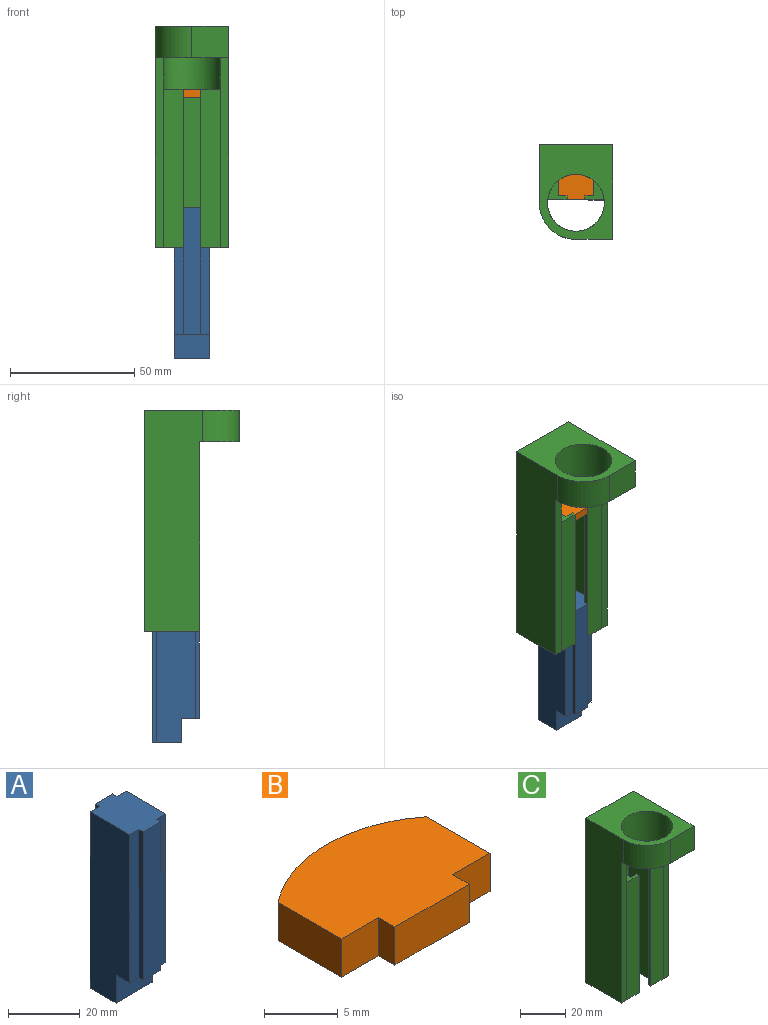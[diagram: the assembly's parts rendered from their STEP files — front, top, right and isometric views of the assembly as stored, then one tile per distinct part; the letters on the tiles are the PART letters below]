
ASSEMBLY  parts=3 mates=2
PART A: 18 faces, bbox 14.2x19x60.3 mm
  f0: plane 60.33x1.63mm, normal (-1,0,0), area 98.1mm2, adj f1,f11,f12,f15
  f1: plane 60.33x3.58mm, normal (0,1,0), area 216mm2, adj f0,f2,f12,f15
  f2: plane 60.33x15.75mm, normal (-1,0,0), area 897.7mm2, adj f1,f3,f12,f13,f14,f15
  f3: plane 50.8x3.58mm, normal (0,-1,0), area 181.9mm2, adj f2,f4,f12,f13
  f4: plane 50.8x1.63mm, normal (-1,0,0), area 82.6mm2, adj f3,f5,f12,f13
  f5: plane 50.8x7.06mm, normal (0,-1,0), area 358.7mm2, adj f4,f6,f12,f13
  f6: plane 50.8x1.63mm, normal (1,0,0), area 82.6mm2, adj f5,f7,f12,f13
  f7: plane 50.8x3.58mm, normal (0,-1,0), area 181.9mm2, adj f6,f8,f12,f13
  f8: plane 60.33x15.75mm, normal (1,0,0), area 897.7mm2, adj f7,f9,f12,f13,f14,f15
  f9: plane 60.33x3.58mm, normal (0,1,0), area 216mm2, adj f8,f10,f12,f15
  f10: plane 60.33x1.63mm, normal (1,0,0), area 98.1mm2, adj f9,f11,f12,f15
  f11: plane 60.33x7.06mm, normal (0,1,0), area 426mm2, adj f0,f10,f12,f15
  f12: plane 19x14.22mm, normal (0,0,1), area 247mm2, adj f0,f1,f2,f3,f4,f5,f6,f7
  f13: plane 14.22x7.11mm, normal (0,0,-1), area 81.6mm2, adj f2,f3,f4,f5,f6,f7,f8,f14
  f14: plane 14.22x9.53mm, normal (0,-1,0), area 135.5mm2, adj f2,f8,f13,f15
  f15: plane 14.22x11.89mm, normal (0,0,-1), area 157.4mm2, adj f0,f1,f2,f8,f9,f10,f11,f14
  f16: cone r=0mm half-angle=59deg, axis (0,0,-1), area 9.2mm2, adj f17
  f17: cylinder r=1.59mm len=9.53mm, axis (0,0,-1), area 95mm2, adj f13,f16
PART B: 10 faces, bbox 14.3x10.2x3.2 mm
  f0: plane 3.18x1.57mm, normal (-1,0,0), area 5mm2, adj f1,f7,f8,f9
  f1: plane 7.14x3.18mm, normal (0,-1,0), area 22.7mm2, adj f0,f2,f8,f9
  f2: plane 3.18x1.57mm, normal (1,0,0), area 5mm2, adj f1,f3,f8,f9
  f3: plane 3.58x3.18mm, normal (0,-1,0), area 11.4mm2, adj f2,f4,f8,f9
  f4: plane 6.06x3.18mm, normal (1,0,0), area 19.2mm2, adj f3,f5,f8,f9
  f5: cylinder r=11.43mm len=14.3mm, axis (0,0,-1), area 49.1mm2, adj f4,f6,f8,f9
  f6: plane 6.08x3.18mm, normal (-1,0,0), area 19.3mm2, adj f5,f7,f8,f9
  f7: plane 3.58x3.18mm, normal (0,-1,0), area 11.4mm2, adj f0,f6,f8,f9
  f8: plane 14.3x10.16mm, normal (0,0,1), area 122.6mm2, adj f0,f1,f2,f3,f4,f5,f6,f7
  f9: plane 14.3x10.16mm, normal (0,0,-1), area 122.6mm2, adj f0,f1,f2,f3,f4,f5,f6,f7
PART C: 27 faces, bbox 29.5x38.1x88.9 mm
  f0: plane 63.5x7.14mm, normal (0,-1,0), area 453.2mm2, adj f4,f5,f17,f26
  f1: plane 63.5x15.88mm, normal (-1,0,0), area 1008.1mm2, adj f6,f17,f20,f21,f26
  f2: plane 63.5x15.88mm, normal (1,0,0), area 1008.1mm2, adj f3,f17,f24,f25,f26
  f3: plane 63.5x3.58mm, normal (0,-1,0), area 227.4mm2, adj f2,f4,f17,f26
  f4: plane 63.5x1.57mm, normal (1,0,0), area 100mm2, adj f0,f3,f17,f26
  f5: plane 63.5x1.57mm, normal (-1,0,0), area 100mm2, adj f0,f6,f17,f26
  f6: plane 63.5x3.58mm, normal (0,-1,0), area 227.4mm2, adj f1,f5,f17,f26
  f7: plane 88.9x23.37mm, normal (-1,0,0), area 1982.6mm2, adj f8,f12,f13,f14,f16,f17
  f8: cylinder r=14.73mm len=14.73mm, axis (0,0,-1), area 293.9mm2, adj f7,f9,f12,f13
  f9: plane 14.73x12.7mm, normal (0,-1,0), area 187.1mm2, adj f8,f10,f12,f13
  f10: plane 88.9x38.1mm, normal (1,0,0), area 2169.7mm2, adj f9,f12,f13,f15,f16,f17
  f11: cylinder r=11.43mm len=25.4mm, axis (0,0,-1), area 1336.4mm2, adj f12,f13,f14,f15,f21,f25,f26
  f12: plane 38.1x29.46mm, normal (0,0,1), area 665.6mm2, adj f7,f8,f9,f10,f11,f16
  f13: plane 29.46x15.98mm, normal (0,0,-1), area 190.5mm2, adj f7,f8,f9,f10,f11,f14,f15
  f14: plane 76.2x3.37mm, normal (0,-1,0), area 256.8mm2, adj f7,f11,f13,f17,f22
  f15: plane 76.2x3.37mm, normal (0,-1,0), area 256.8mm2, adj f10,f11,f13,f17,f19
  f16: plane 88.9x29.46mm, normal (0,1,0), area 2619.3mm2, adj f7,f10,f12,f17
  f17: plane 29.46x22.12mm, normal (0,0,-1), area 402mm2, adj f0,f1,f2,f3,f4,f5,f6,f7
  f18: plane 63.5x1.57mm, normal (-1,0,0), area 100mm2, adj f17,f19,f20,f21
  f19: plane 63.5x7.78mm, normal (0,-1,0), area 494.1mm2, adj f15,f17,f18,f21
  f20: plane 63.5x3.58mm, normal (0,1,0), area 227.4mm2, adj f1,f17,f18,f21
  f21: plane 7.78x7.66mm, normal (0,0,1), area 26.8mm2, adj f1,f11,f18,f19,f20
  f22: plane 63.5x7.81mm, normal (0,-1,0), area 495.7mm2, adj f14,f17,f23,f25
  f23: plane 63.5x1.57mm, normal (1,0,0), area 100mm2, adj f17,f22,f24,f25
  f24: plane 63.5x3.58mm, normal (0,1,0), area 227.4mm2, adj f2,f17,f23,f25
  f25: plane 7.81x7.68mm, normal (0,0,1), area 27mm2, adj f2,f11,f22,f23,f24
  f26: plane 14.3x11.39mm, normal (0,0,-1), area 126.9mm2, adj f0,f1,f2,f3,f4,f5,f6,f11
PLACE A rot(axis=(0,0,-1),0.2deg) t=(8.63,-1.08,-20.01)mm
PLACE B t=(8.55,-7.6,14.92)mm
PLACE C rot(axis=(0,0,-1),0.2deg) t=(8.56,-7.61,14.92)mm fixed
MATE slider A.f15 <-> C.f17  axis (0,0,1) through (15.77,6.77,-29.53)mm
MATE fastened C.f22 <-> B.f1  axis (0,-1,0) through (4.99,-10.65,78.42)mm
